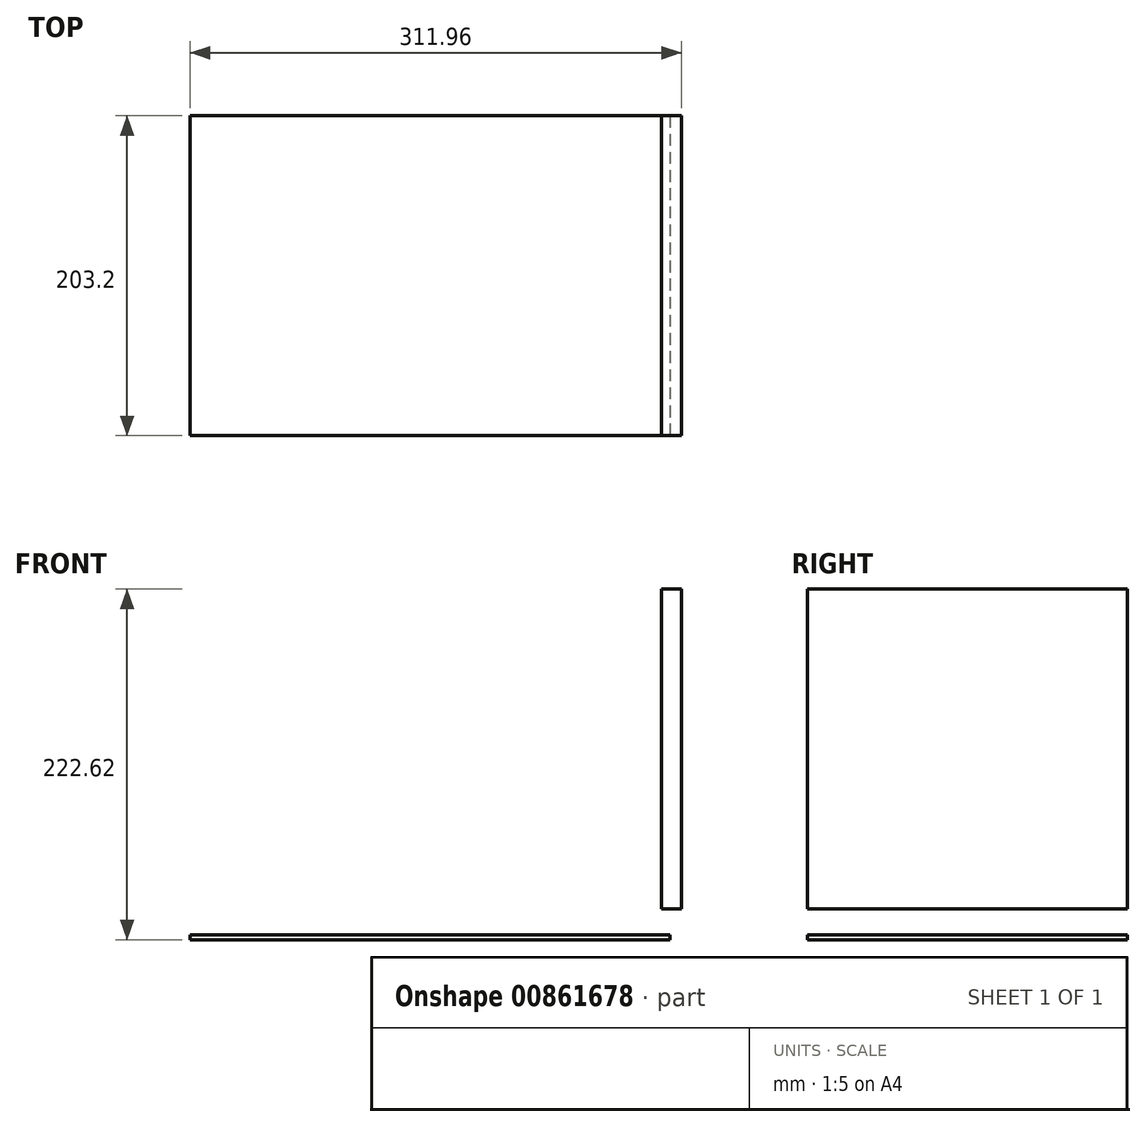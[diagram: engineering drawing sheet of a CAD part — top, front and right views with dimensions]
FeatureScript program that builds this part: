
annotation { "Feature Type Name" : "Feature", "Feature Type Description" : "" }
export const myFeature = defineFeature(function(context is Context, id is Id, definition is map)
    precondition{}
    {
        {
            var Q0;
            Q0=qCreatedBy(makeId("Top.planeOp"),FACE);
            var sketch = newSketch(context, id + "F0", { "sketchPlane" : qUnion([Q0])});
            skLineSegment(sketch, "E0.bottom", {"start": v(152.4, 101.6) * mm, "end": v(-152.4, 101.6) * mm});
            skLineSegment(sketch, "E0.top", {"start": v(152.4, -101.6) * mm, "end": v(-152.4, -101.6) * mm});
            skLineSegment(sketch, "E0.left", {"start": v(152.4, 101.6) * mm, "end": v(152.4, -101.6) * mm});
            skLineSegment(sketch, "E0.right", {"start": v(-152.4, 101.6) * mm, "end": v(-152.4, -101.6) * mm});
            skPoint(sketch, "E0.middle", {"position": v(0, 0) * mm});
            skSolve(sketch);
        }
        {
            var Q0;
            Q0=makeQuery(id+"F0.imprint","IMPRINT",FACE,{"disambiguationData":[TD([[makeQuery(id+"F0.imprint","IMPRINT",EDGE,{"derivedFrom":sQuery(id+"F0.wireOp",EDGE,"E0.bottom")}),1.0]])]});
            var Q1;
            Q1 = qSketchRegion(id + "F2", true);
            extrude(context, id + "F1", {"entities" : qUnion([Q0, Q1]), "depth" : 3.17 * mm, "offsetDistance" : 25.4 * mm});
        }
        {
            var Q0;
            Q0=qCreatedBy(makeId("Front.planeOp"),FACE);
            var sketch = newSketch(context, id + "F2", { "sketchPlane" : qUnion([Q0])});
            skLineSegment(sketch, "E1.bottom", {"start": v(159.56, 19.42) * mm, "end": v(146.86, 19.42) * mm});
            skLineSegment(sketch, "E1.top", {"start": v(159.56, 222.62) * mm, "end": v(146.86, 222.62) * mm});
            skLineSegment(sketch, "E1.left", {"start": v(159.56, 19.42) * mm, "end": v(159.56, 222.62) * mm});
            skLineSegment(sketch, "E1.right", {"start": v(146.86, 19.42) * mm, "end": v(146.86, 222.62) * mm});
            skPoint(sketch, "E1.middle", {"position": v(153.2, 121.02) * mm});
            skSolve(sketch);
        }
        {
            var Q0;
            Q0 = qSketchRegion(id + "F2", true);
            extrude(context, id + "F3", {"entities" : qUnion([Q0]), "endBound" : BoundingType.SYMMETRIC, "depth" : 203.2 * mm, "offsetDistance" : 25.4 * mm});
        }
    });
